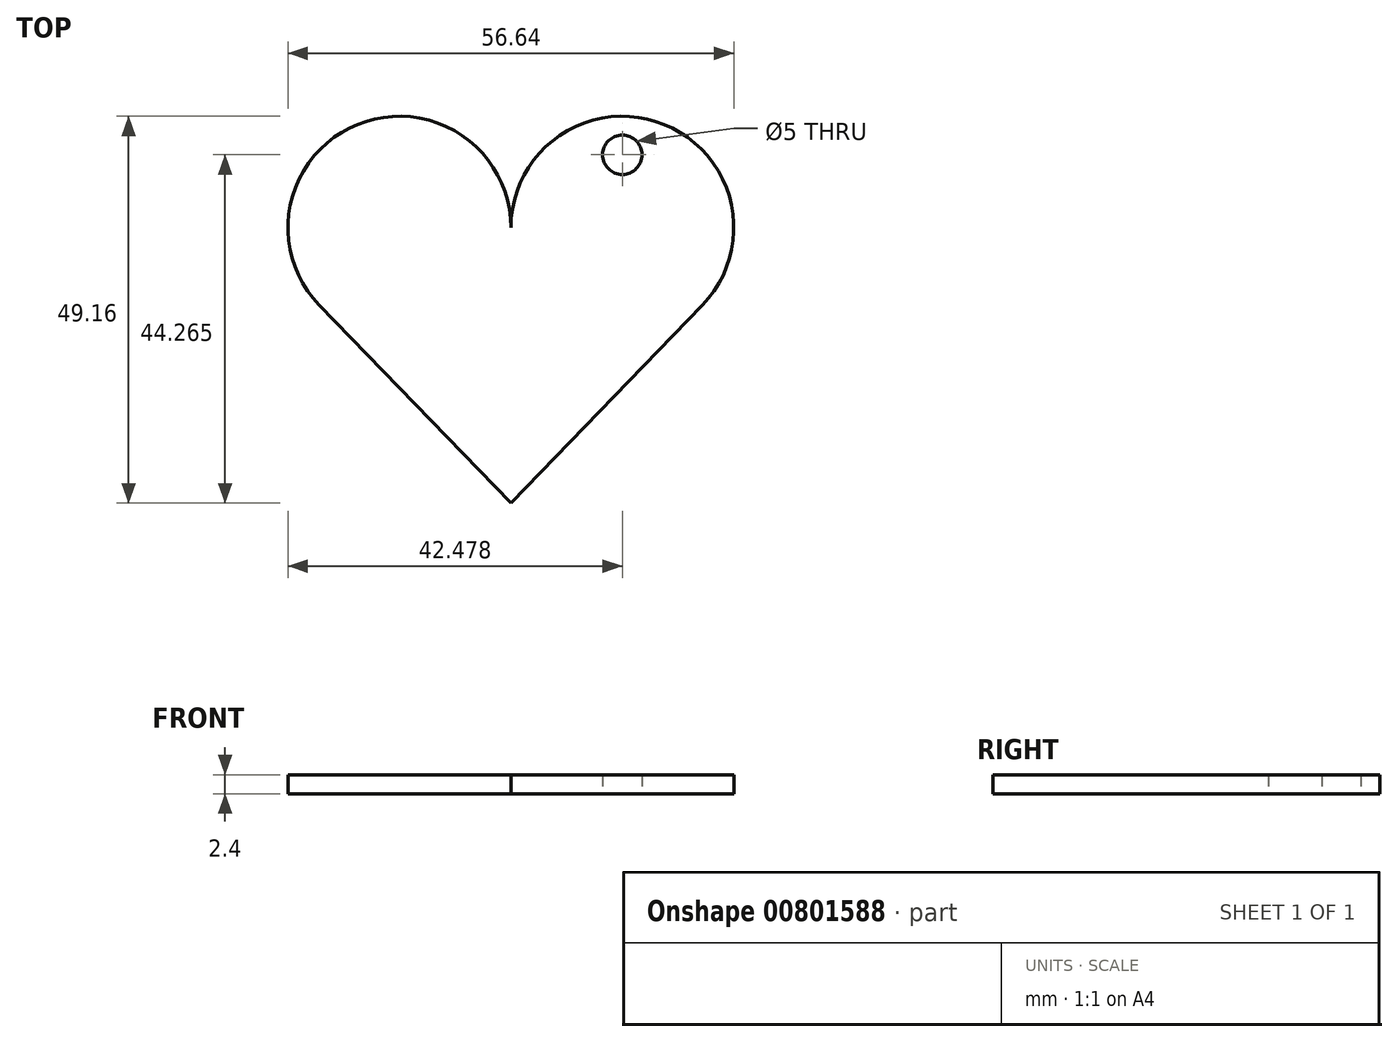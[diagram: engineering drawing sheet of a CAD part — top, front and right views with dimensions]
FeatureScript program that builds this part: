
annotation { "Feature Type Name" : "Feature", "Feature Type Description" : "" }
export const myFeature = defineFeature(function(context is Context, id is Id, definition is map)
    precondition{}
    {
        {
            var Q0;
            Q0=qCreatedBy(makeId("Top.planeOp"),FACE);
            var sketch = newSketch(context, id + "F0", { "sketchPlane" : qUnion([Q0])});
            skPoint(sketch, "E0.start.orphan", {"position": v(-73.01, 0) * mm});
            skLineSegment(sketch, "E1", {"start": v(14.16, 0) * mm, "end": v(28.32, 0) * mm});
            skArc(sketch, "E2", {"start": v(0, 0) * mm, "mid": v(-19.47, 13.13) * mm, "end": v(-24.33, -9.84) * mm});
            skArc(sketch, "E3", {"start": v(24.33, -9.84) * mm, "mid": v(19.47, 13.13) * mm, "end": v(0, 0) * mm});
            skLineSegment(sketch, "E4", {"start": v(0, 0) * mm, "end": v(0, -35) * mm});
            skLineSegment(sketch, "E5", {"start": v(0, -35) * mm, "end": v(24.33, -9.84) * mm});
            skLineSegment(sketch, "E6", {"start": v(0, -35) * mm, "end": v(-24.33, -9.84) * mm});
            skPoint(sketch, "E7.end.orphan", {"position": v(39.45, 0) * mm});
            skPoint(sketch, "E8.orphan", {"position": v(0, 0) * mm});
            skPoint(sketch, "E9.MirrorCS.end.orphan", {"position": v(-28.32, 0) * mm});
            skCircle(sketch, "E10", {"center": v(14.16, 9.26) * mm, "radius": 2.5 * mm});
            skSolve(sketch);
        }
        {
            var Q0;
            Q0=makeQuery(id+"F0.imprint","IMPRINT",FACE,{"disambiguationData":[TD([[makeQuery(id+"F0.imprint","IMPRINT",EDGE,{"derivedFrom":sQuery(id+"F0.wireOp",EDGE,"E2")}),1.0]])]});
            var Q1;
            {var subQ1=sQuery(id+"F0.wireOp",EDGE,"E4");Q1=makeQuery(id+"F0.imprint","IMPRINT",FACE,{"disambiguationData":[TD([[makeQuery(id+"F0.imprint","IMPRINT",EDGE,{"derivedFrom":subQ1}),1.0]])]});}
            extrude(context, id + "F1", {"entities" : qUnion([Q0, Q1]), "depth" : 2.4 * mm, "offsetDistance" : 25 * mm});
        }
    });
